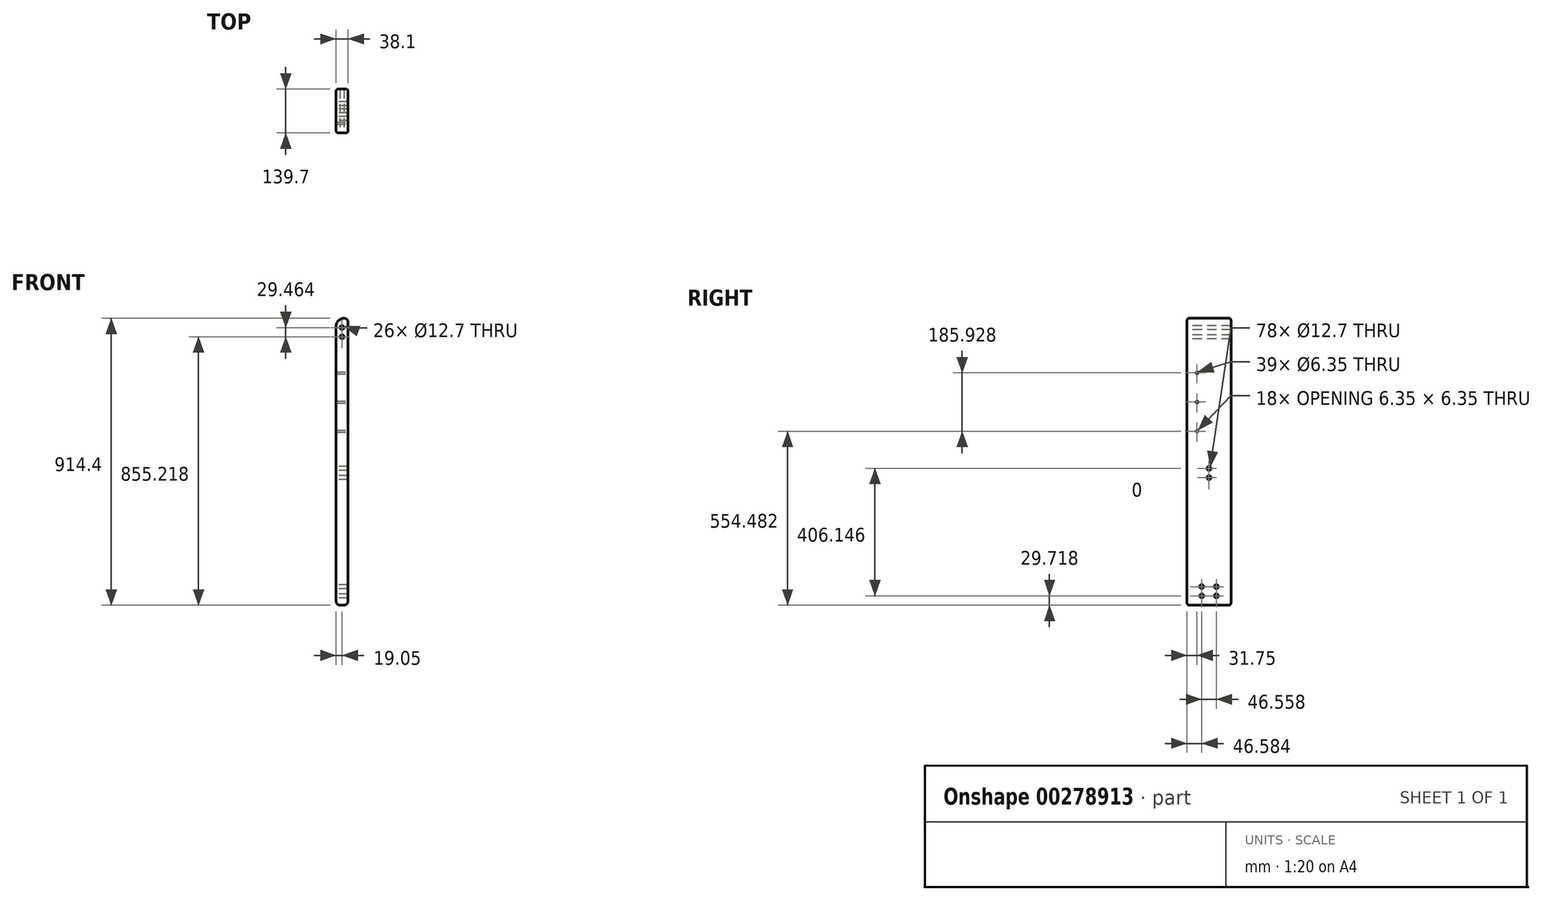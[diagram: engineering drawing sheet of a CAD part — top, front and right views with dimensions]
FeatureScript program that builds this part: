
annotation { "Feature Type Name" : "Feature", "Feature Type Description" : "" }
export const myFeature = defineFeature(function(context is Context, id is Id, definition is map)
    precondition{}
    {
        {
            var Q0;
            Q0=qCreatedBy(makeId("Front.planeOp"),FACE);
            var sketch = newSketch(context, id + "F0", { "sketchPlane" : qUnion([Q0])});
            skLineSegment(sketch, "E0.bottom", {"start": v(19.05, 457.2) * mm, "end": v(-19.05, 457.2) * mm});
            skLineSegment(sketch, "E0.top", {"start": v(19.05, -457.2) * mm, "end": v(-19.05, -457.2) * mm});
            skLineSegment(sketch, "E0.left", {"start": v(19.05, 457.2) * mm, "end": v(19.05, -457.2) * mm});
            skLineSegment(sketch, "E0.right", {"start": v(-19.05, 457.2) * mm, "end": v(-19.05, -457.2) * mm});
            skPoint(sketch, "E0.middle", {"position": v(0, 0) * mm});
            skCircle(sketch, "E1", {"center": v(0, 427.48) * mm, "radius": 6.35 * mm});
            skCircle(sketch, "E2", {"center": v(0, 398.02) * mm, "radius": 6.35 * mm});
            skSolve(sketch);
        }
        {
            var Q0;
            Q0=qSketchRegion(id+"F0",true);
            extrude(context, id + "F1", {"entities" : qUnion([Q0]), "oppositeDirection" : true, "depth" : 139.7 * mm});
        }
        {
            var Q0;
            Q0=makeQuery(id+"F1.opExtrude","SWEPT_FACE",FACE,{"disambiguationData":[OSD([sQuery(id+"F0.wireOp",EDGE,"E0.right")])]});
            var sketch = newSketch(context, id + "F2", { "sketchPlane" : qUnion([Q0])});
            skCircle(sketch, "E3", {"center": v(-93.14, -427.48) * mm, "radius": 6.35 * mm});
            skCircle(sketch, "E4.0.1.0", {"center": v(-93.14, -398.02) * mm, "radius": 6.35 * mm});
            skCircle(sketch, "E4.1.0.0", {"center": v(-46.58, -427.48) * mm, "radius": 6.35 * mm});
            skCircle(sketch, "E4.1.1.0", {"center": v(-46.58, -398.02) * mm, "radius": 6.35 * mm});
            skLineSegment(sketch, "E4.direction1", {"start": v(-93.14, -427.48) * mm, "end": v(-46.58, -427.48) * mm, "construction": true});
            skLineSegment(sketch, "E4.direction2", {"start": v(-93.14, -427.48) * mm, "end": v(-93.14, -398.02) * mm, "construction": true});
            skSolve(sketch);
        }
        {
            var Q0;
            Q0=qSketchRegion(id+"F2",true);
            extrude(context, id + "F3", {"entities" : qUnion([Q0]), "operationType" : NewBodyOperationType.REMOVE, "oppositeDirection" : true, "depth" : 38.1 * mm});
        }
        {
            var Q0;
            Q0=makeQuery(id+"F1.opExtrude","SWEPT_FACE",FACE,{"disambiguationData":[OSD([sQuery(id+"F0.wireOp",EDGE,"E0.right")])]});
            var sketch = newSketch(context, id + "F6", { "sketchPlane" : qUnion([Q0])});
            skCircle(sketch, "E5", {"center": v(-69.85, -21.34) * mm, "radius": 6.35 * mm});
            skCircle(sketch, "E6.0.1.0", {"center": v(-69.85, -50.8) * mm, "radius": 6.35 * mm});
            skLineSegment(sketch, "E6.direction1", {"start": v(-69.85, -21.34) * mm, "end": v(-37.33, -21.34) * mm, "construction": true});
            skLineSegment(sketch, "E6.direction2", {"start": v(-69.85, -21.34) * mm, "end": v(-69.85, -50.8) * mm, "construction": true});
            skPoint(sketch, "E7", {"position": v(-31.75, 368.3) * mm});
            skPoint(sketch, "E8", {"position": v(-31.75, 283.21) * mm});
            skPoint(sketch, "E9", {"position": v(-31.75, 190.25) * mm});
            skPoint(sketch, "E10", {"position": v(-31.75, 97.28) * mm});
            skSolve(sketch);
        }
        {
            var Q0;
            Q0=qSketchRegion(id+"F6",true);
            extrude(context, id + "F7", {"entities" : qUnion([Q0]), "operationType" : NewBodyOperationType.REMOVE, "oppositeDirection" : true, "depth" : 38.1 * mm});
        }
        {
            var Q0;
            Q0=sQuery(id+"F6.wireOp",VERTEX,"E8");
            var Q1;
            Q1=sQuery(id+"F6.wireOp",VERTEX,"E9");
            var Q2;
            Q2=sQuery(id+"F6.wireOp",VERTEX,"E10");
            var Q3;
            Q3=makeQuery(id+"F1.opExtrude","SWEPT_BODY",BODY,{"disambiguationData":[OSD([sQuery(id+"F0.wireOp",EDGE,"E0.bottom"),sQuery(id+"F0.wireOp",EDGE,"E0.top"),sQuery(id+"F0.wireOp",EDGE,"E0.left"),sQuery(id+"F0.wireOp",EDGE,"E0.right"),sQuery(id+"F0.wireOp",EDGE,"E1"),sQuery(id+"F0.wireOp",EDGE,"E2")])]});
            hole(context, id + "F8", {"style" : HoleStyle.SIMPLE, "endStyle" : HoleEndStyle.THROUGH, "holeDiameter" : 6.35 * mm, "tappedDepth" : 12.7 * mm, "tapClearance" : 3, "locations" : qUnion([Q0, Q1, Q2]), "scope" : qUnion([Q3]), "startStyle" : HoleStartStyle.PART});
        }
        {
            var Q0;
            Q0=makeQuery(id+"F1.opExtrude","SWEPT_EDGE",EDGE,{"disambiguationData":[OSD([sQuery(id+"F0.wireOp",EDGE,"E0.bottom"),sQuery(id+"F0.wireOp",EDGE,"E0.left")])]});
            var Q1;
            Q1=makeQuery(id+"F1.opExtrude","SWEPT_EDGE",EDGE,{"disambiguationData":[OSD([sQuery(id+"F0.wireOp",EDGE,"E0.top"),sQuery(id+"F0.wireOp",EDGE,"E0.right")])]});
            var Q2;
            Q2=makeQuery(id+"F1.opExtrude","SWEPT_EDGE",EDGE,{"disambiguationData":[OSD([sQuery(id+"F0.wireOp",EDGE,"E0.top"),sQuery(id+"F0.wireOp",EDGE,"E0.left")])]});
            fillet(context, id + "F4", {"entities" : qUnion([Q0, Q1, Q2]), "radius" : 12.7 * mm, "tangentPropagation" : true, "allowEdgeOverflow" : false});
        }
        {
            var Q0;
            Q0=makeQuery(id+"F1.opExtrude","CAP_EDGE",EDGE,{"disambiguationData":[OSD([sQuery(id+"F0.wireOp",EDGE,"E0.right")])],"isStart":true});
            var Q1;
            Q1=makeQuery(id+"F1.opExtrude","CAP_EDGE",EDGE,{"disambiguationData":[OSD([sQuery(id+"F0.wireOp",EDGE,"E0.left")])],"isStart":true});
            var Q2;
            Q2=makeQuery(id+"F1.opExtrude","CAP_EDGE",EDGE,{"disambiguationData":[OSD([sQuery(id+"F0.wireOp",EDGE,"E0.left")])],"isStart":false});
            fillet(context, id + "F5", {"entities" : qUnion([Q0, Q1, Q2]), "radius" : 6.35 * mm, "tangentPropagation" : true, "allowEdgeOverflow" : false});
        }
        {
            var Q0;
            Q0=makeQuery(id+"F1.opExtrude","SWEPT_EDGE",EDGE,{"disambiguationData":[OSD([sQuery(id+"F0.wireOp",EDGE,"E0.bottom"),sQuery(id+"F0.wireOp",EDGE,"E0.right")])]});
            fillet(context, id + "F9", {"entities" : qUnion([Q0]), "radius" : 25.4 * mm, "tangentPropagation" : true, "allowEdgeOverflow" : false});
        }
    });
